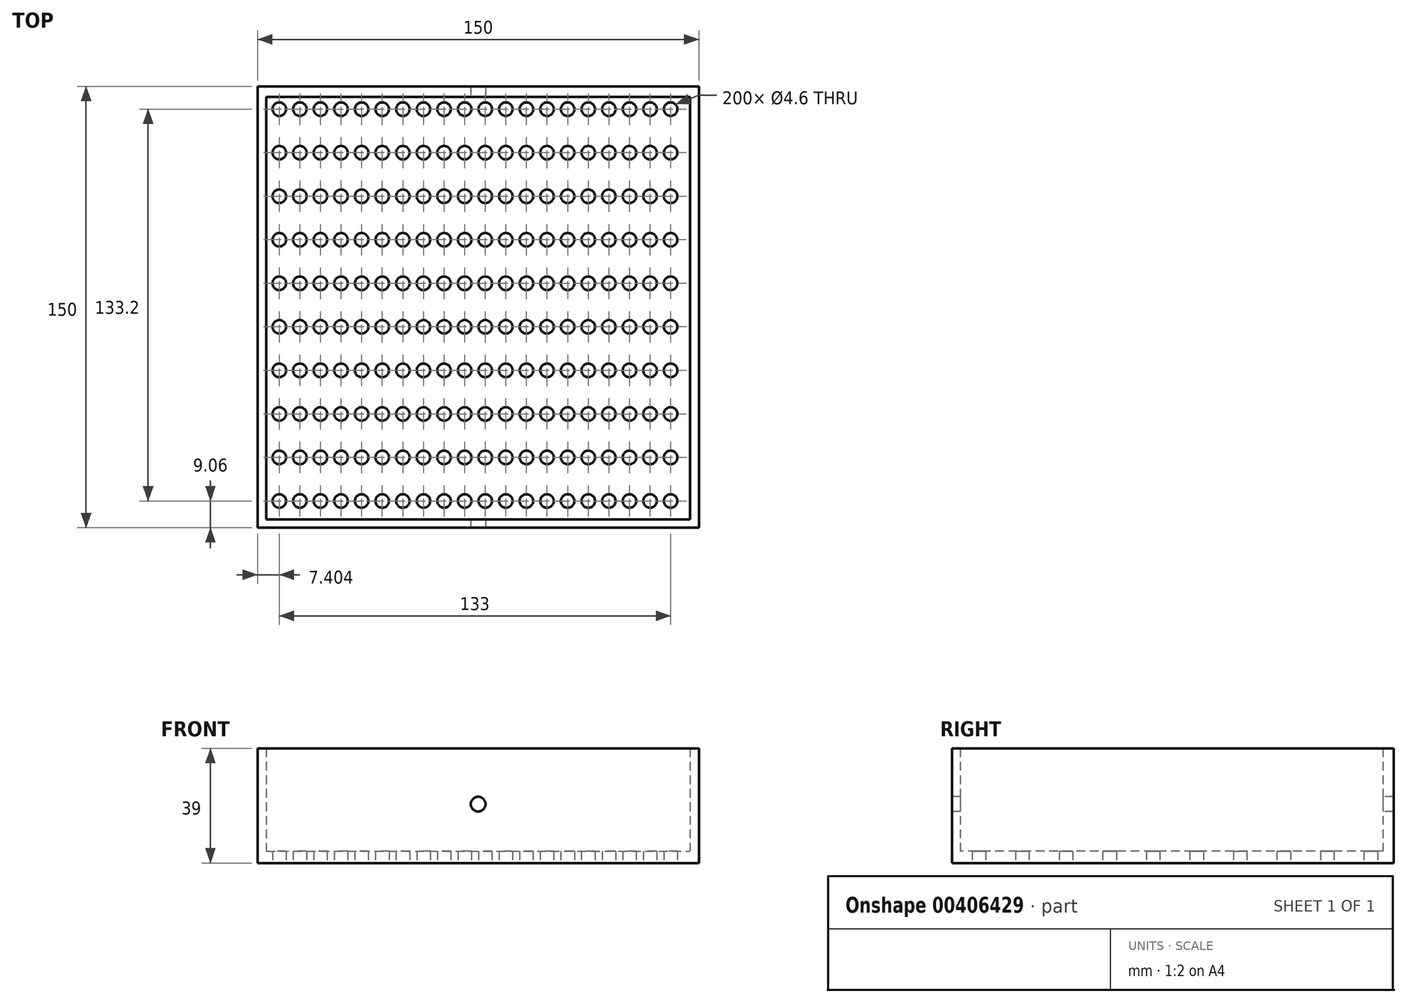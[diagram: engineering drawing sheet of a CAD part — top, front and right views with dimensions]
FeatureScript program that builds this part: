
annotation { "Feature Type Name" : "Feature", "Feature Type Description" : "" }
export const myFeature = defineFeature(function(context is Context, id is Id, definition is map)
    precondition{}
    {
        {
            var Q0;
            Q0=qCreatedBy(makeId("Top.planeOp"),FACE);
            var sketch = newSketch(context, id + "F0", { "sketchPlane" : qUnion([Q0])});
            skLineSegment(sketch, "E0.bottom", {"start": v(75, 75) * mm, "end": v(-75, 75) * mm});
            skLineSegment(sketch, "E0.top", {"start": v(75, -75) * mm, "end": v(-75, -75) * mm});
            skLineSegment(sketch, "E0.left", {"start": v(75, 75) * mm, "end": v(75, -75) * mm});
            skLineSegment(sketch, "E0.right", {"start": v(-75, 75) * mm, "end": v(-75, -75) * mm});
            skPoint(sketch, "E0.middle", {"position": v(0, 0) * mm});
            skCircle(sketch, "E1", {"center": v(-67.6, 67.26) * mm, "radius": 2.3 * mm});
            skCircle(sketch, "E2.0.1.0", {"center": v(-67.6, 52.46) * mm, "radius": 2.3 * mm});
            skCircle(sketch, "E2.0.2.0", {"center": v(-67.6, 37.66) * mm, "radius": 2.3 * mm});
            skCircle(sketch, "E2.0.3.0", {"center": v(-67.6, 22.86) * mm, "radius": 2.3 * mm});
            skCircle(sketch, "E2.0.4.0", {"center": v(-67.6, 8.06) * mm, "radius": 2.3 * mm});
            skCircle(sketch, "E2.0.5.0", {"center": v(-67.6, -6.74) * mm, "radius": 2.3 * mm});
            skCircle(sketch, "E2.0.6.0", {"center": v(-67.6, -21.54) * mm, "radius": 2.3 * mm});
            skCircle(sketch, "E2.0.7.0", {"center": v(-67.6, -36.34) * mm, "radius": 2.3 * mm});
            skCircle(sketch, "E2.0.8.0", {"center": v(-67.6, -51.14) * mm, "radius": 2.3 * mm});
            skCircle(sketch, "E2.0.9.0", {"center": v(-67.6, -65.94) * mm, "radius": 2.3 * mm});
            skCircle(sketch, "E2.1.0.0", {"center": v(-60.6, 67.26) * mm, "radius": 2.3 * mm});
            skCircle(sketch, "E2.1.1.0", {"center": v(-60.6, 52.46) * mm, "radius": 2.3 * mm});
            skCircle(sketch, "E2.1.2.0", {"center": v(-60.6, 37.66) * mm, "radius": 2.3 * mm});
            skCircle(sketch, "E2.1.3.0", {"center": v(-60.6, 22.86) * mm, "radius": 2.3 * mm});
            skCircle(sketch, "E2.1.4.0", {"center": v(-60.6, 8.06) * mm, "radius": 2.3 * mm});
            skCircle(sketch, "E2.1.5.0", {"center": v(-60.6, -6.74) * mm, "radius": 2.3 * mm});
            skCircle(sketch, "E2.1.6.0", {"center": v(-60.6, -21.54) * mm, "radius": 2.3 * mm});
            skCircle(sketch, "E2.1.7.0", {"center": v(-60.6, -36.34) * mm, "radius": 2.3 * mm});
            skCircle(sketch, "E2.1.8.0", {"center": v(-60.6, -51.14) * mm, "radius": 2.3 * mm});
            skCircle(sketch, "E2.1.9.0", {"center": v(-60.6, -65.94) * mm, "radius": 2.3 * mm});
            skCircle(sketch, "E2.2.0.0", {"center": v(-53.6, 67.26) * mm, "radius": 2.3 * mm});
            skCircle(sketch, "E2.2.1.0", {"center": v(-53.6, 52.46) * mm, "radius": 2.3 * mm});
            skCircle(sketch, "E2.2.2.0", {"center": v(-53.6, 37.66) * mm, "radius": 2.3 * mm});
            skCircle(sketch, "E2.2.3.0", {"center": v(-53.6, 22.86) * mm, "radius": 2.3 * mm});
            skCircle(sketch, "E2.2.4.0", {"center": v(-53.6, 8.06) * mm, "radius": 2.3 * mm});
            skCircle(sketch, "E2.2.5.0", {"center": v(-53.6, -6.74) * mm, "radius": 2.3 * mm});
            skCircle(sketch, "E2.2.6.0", {"center": v(-53.6, -21.54) * mm, "radius": 2.3 * mm});
            skCircle(sketch, "E2.2.7.0", {"center": v(-53.6, -36.34) * mm, "radius": 2.3 * mm});
            skCircle(sketch, "E2.2.8.0", {"center": v(-53.6, -51.14) * mm, "radius": 2.3 * mm});
            skCircle(sketch, "E2.2.9.0", {"center": v(-53.6, -65.94) * mm, "radius": 2.3 * mm});
            skCircle(sketch, "E2.3.0.0", {"center": v(-46.6, 67.26) * mm, "radius": 2.3 * mm});
            skCircle(sketch, "E2.3.1.0", {"center": v(-46.6, 52.46) * mm, "radius": 2.3 * mm});
            skCircle(sketch, "E2.3.2.0", {"center": v(-46.6, 37.66) * mm, "radius": 2.3 * mm});
            skCircle(sketch, "E2.3.3.0", {"center": v(-46.6, 22.86) * mm, "radius": 2.3 * mm});
            skCircle(sketch, "E2.3.4.0", {"center": v(-46.6, 8.06) * mm, "radius": 2.3 * mm});
            skCircle(sketch, "E2.3.5.0", {"center": v(-46.6, -6.74) * mm, "radius": 2.3 * mm});
            skCircle(sketch, "E2.3.6.0", {"center": v(-46.6, -21.54) * mm, "radius": 2.3 * mm});
            skCircle(sketch, "E2.3.7.0", {"center": v(-46.6, -36.34) * mm, "radius": 2.3 * mm});
            skCircle(sketch, "E2.3.8.0", {"center": v(-46.6, -51.14) * mm, "radius": 2.3 * mm});
            skCircle(sketch, "E2.3.9.0", {"center": v(-46.6, -65.94) * mm, "radius": 2.3 * mm});
            skCircle(sketch, "E2.4.0.0", {"center": v(-39.6, 67.26) * mm, "radius": 2.3 * mm});
            skCircle(sketch, "E2.4.1.0", {"center": v(-39.6, 52.46) * mm, "radius": 2.3 * mm});
            skCircle(sketch, "E2.4.2.0", {"center": v(-39.6, 37.66) * mm, "radius": 2.3 * mm});
            skCircle(sketch, "E2.4.3.0", {"center": v(-39.6, 22.86) * mm, "radius": 2.3 * mm});
            skCircle(sketch, "E2.4.4.0", {"center": v(-39.6, 8.06) * mm, "radius": 2.3 * mm});
            skCircle(sketch, "E2.4.5.0", {"center": v(-39.6, -6.74) * mm, "radius": 2.3 * mm});
            skCircle(sketch, "E2.4.6.0", {"center": v(-39.6, -21.54) * mm, "radius": 2.3 * mm});
            skCircle(sketch, "E2.4.7.0", {"center": v(-39.6, -36.34) * mm, "radius": 2.3 * mm});
            skCircle(sketch, "E2.4.8.0", {"center": v(-39.6, -51.14) * mm, "radius": 2.3 * mm});
            skCircle(sketch, "E2.4.9.0", {"center": v(-39.6, -65.94) * mm, "radius": 2.3 * mm});
            skCircle(sketch, "E2.5.0.0", {"center": v(-32.6, 67.26) * mm, "radius": 2.3 * mm});
            skCircle(sketch, "E2.5.1.0", {"center": v(-32.6, 52.46) * mm, "radius": 2.3 * mm});
            skCircle(sketch, "E2.5.2.0", {"center": v(-32.6, 37.66) * mm, "radius": 2.3 * mm});
            skCircle(sketch, "E2.5.3.0", {"center": v(-32.6, 22.86) * mm, "radius": 2.3 * mm});
            skCircle(sketch, "E2.5.4.0", {"center": v(-32.6, 8.06) * mm, "radius": 2.3 * mm});
            skCircle(sketch, "E2.5.5.0", {"center": v(-32.6, -6.74) * mm, "radius": 2.3 * mm});
            skCircle(sketch, "E2.5.6.0", {"center": v(-32.6, -21.54) * mm, "radius": 2.3 * mm});
            skCircle(sketch, "E2.5.7.0", {"center": v(-32.6, -36.34) * mm, "radius": 2.3 * mm});
            skCircle(sketch, "E2.5.8.0", {"center": v(-32.6, -51.14) * mm, "radius": 2.3 * mm});
            skCircle(sketch, "E2.5.9.0", {"center": v(-32.6, -65.94) * mm, "radius": 2.3 * mm});
            skCircle(sketch, "E2.6.0.0", {"center": v(-25.6, 67.26) * mm, "radius": 2.3 * mm});
            skCircle(sketch, "E2.6.1.0", {"center": v(-25.6, 52.46) * mm, "radius": 2.3 * mm});
            skCircle(sketch, "E2.6.2.0", {"center": v(-25.6, 37.66) * mm, "radius": 2.3 * mm});
            skCircle(sketch, "E2.6.3.0", {"center": v(-25.6, 22.86) * mm, "radius": 2.3 * mm});
            skCircle(sketch, "E2.6.4.0", {"center": v(-25.6, 8.06) * mm, "radius": 2.3 * mm});
            skCircle(sketch, "E2.6.5.0", {"center": v(-25.6, -6.74) * mm, "radius": 2.3 * mm});
            skCircle(sketch, "E2.6.6.0", {"center": v(-25.6, -21.54) * mm, "radius": 2.3 * mm});
            skCircle(sketch, "E2.6.7.0", {"center": v(-25.6, -36.34) * mm, "radius": 2.3 * mm});
            skCircle(sketch, "E2.6.8.0", {"center": v(-25.6, -51.14) * mm, "radius": 2.3 * mm});
            skCircle(sketch, "E2.6.9.0", {"center": v(-25.6, -65.94) * mm, "radius": 2.3 * mm});
            skCircle(sketch, "E2.7.0.0", {"center": v(-18.6, 67.26) * mm, "radius": 2.3 * mm});
            skCircle(sketch, "E2.7.1.0", {"center": v(-18.6, 52.46) * mm, "radius": 2.3 * mm});
            skCircle(sketch, "E2.7.2.0", {"center": v(-18.6, 37.66) * mm, "radius": 2.3 * mm});
            skCircle(sketch, "E2.7.3.0", {"center": v(-18.6, 22.86) * mm, "radius": 2.3 * mm});
            skCircle(sketch, "E2.7.4.0", {"center": v(-18.6, 8.06) * mm, "radius": 2.3 * mm});
            skCircle(sketch, "E2.7.5.0", {"center": v(-18.6, -6.74) * mm, "radius": 2.3 * mm});
            skCircle(sketch, "E2.7.6.0", {"center": v(-18.6, -21.54) * mm, "radius": 2.3 * mm});
            skCircle(sketch, "E2.7.7.0", {"center": v(-18.6, -36.34) * mm, "radius": 2.3 * mm});
            skCircle(sketch, "E2.7.8.0", {"center": v(-18.6, -51.14) * mm, "radius": 2.3 * mm});
            skCircle(sketch, "E2.7.9.0", {"center": v(-18.6, -65.94) * mm, "radius": 2.3 * mm});
            skCircle(sketch, "E2.8.0.0", {"center": v(-11.6, 67.26) * mm, "radius": 2.3 * mm});
            skCircle(sketch, "E2.8.1.0", {"center": v(-11.6, 52.46) * mm, "radius": 2.3 * mm});
            skCircle(sketch, "E2.8.2.0", {"center": v(-11.6, 37.66) * mm, "radius": 2.3 * mm});
            skCircle(sketch, "E2.8.3.0", {"center": v(-11.6, 22.86) * mm, "radius": 2.3 * mm});
            skCircle(sketch, "E2.8.4.0", {"center": v(-11.6, 8.06) * mm, "radius": 2.3 * mm});
            skCircle(sketch, "E2.8.5.0", {"center": v(-11.6, -6.74) * mm, "radius": 2.3 * mm});
            skCircle(sketch, "E2.8.6.0", {"center": v(-11.6, -21.54) * mm, "radius": 2.3 * mm});
            skCircle(sketch, "E2.8.7.0", {"center": v(-11.6, -36.34) * mm, "radius": 2.3 * mm});
            skCircle(sketch, "E2.8.8.0", {"center": v(-11.6, -51.14) * mm, "radius": 2.3 * mm});
            skCircle(sketch, "E2.8.9.0", {"center": v(-11.6, -65.94) * mm, "radius": 2.3 * mm});
            skCircle(sketch, "E2.9.0.0", {"center": v(-4.6, 67.26) * mm, "radius": 2.3 * mm});
            skCircle(sketch, "E2.9.1.0", {"center": v(-4.6, 52.46) * mm, "radius": 2.3 * mm});
            skCircle(sketch, "E2.9.2.0", {"center": v(-4.6, 37.66) * mm, "radius": 2.3 * mm});
            skCircle(sketch, "E2.9.3.0", {"center": v(-4.6, 22.86) * mm, "radius": 2.3 * mm});
            skCircle(sketch, "E2.9.4.0", {"center": v(-4.6, 8.06) * mm, "radius": 2.3 * mm});
            skCircle(sketch, "E2.9.5.0", {"center": v(-4.6, -6.74) * mm, "radius": 2.3 * mm});
            skCircle(sketch, "E2.9.6.0", {"center": v(-4.6, -21.54) * mm, "radius": 2.3 * mm});
            skCircle(sketch, "E2.9.7.0", {"center": v(-4.6, -36.34) * mm, "radius": 2.3 * mm});
            skCircle(sketch, "E2.9.8.0", {"center": v(-4.6, -51.14) * mm, "radius": 2.3 * mm});
            skCircle(sketch, "E2.9.9.0", {"center": v(-4.6, -65.94) * mm, "radius": 2.3 * mm});
            skCircle(sketch, "E2.10.0.0", {"center": v(2.4, 67.26) * mm, "radius": 2.3 * mm});
            skCircle(sketch, "E2.10.1.0", {"center": v(2.4, 52.46) * mm, "radius": 2.3 * mm});
            skCircle(sketch, "E2.10.2.0", {"center": v(2.4, 37.66) * mm, "radius": 2.3 * mm});
            skCircle(sketch, "E2.10.3.0", {"center": v(2.4, 22.86) * mm, "radius": 2.3 * mm});
            skCircle(sketch, "E2.10.4.0", {"center": v(2.4, 8.06) * mm, "radius": 2.3 * mm});
            skCircle(sketch, "E2.10.5.0", {"center": v(2.4, -6.74) * mm, "radius": 2.3 * mm});
            skCircle(sketch, "E2.10.6.0", {"center": v(2.4, -21.54) * mm, "radius": 2.3 * mm});
            skCircle(sketch, "E2.10.7.0", {"center": v(2.4, -36.34) * mm, "radius": 2.3 * mm});
            skCircle(sketch, "E2.10.8.0", {"center": v(2.4, -51.14) * mm, "radius": 2.3 * mm});
            skCircle(sketch, "E2.10.9.0", {"center": v(2.4, -65.94) * mm, "radius": 2.3 * mm});
            skCircle(sketch, "E2.11.0.0", {"center": v(9.4, 67.26) * mm, "radius": 2.3 * mm});
            skCircle(sketch, "E2.11.1.0", {"center": v(9.4, 52.46) * mm, "radius": 2.3 * mm});
            skCircle(sketch, "E2.11.2.0", {"center": v(9.4, 37.66) * mm, "radius": 2.3 * mm});
            skCircle(sketch, "E2.11.3.0", {"center": v(9.4, 22.86) * mm, "radius": 2.3 * mm});
            skCircle(sketch, "E2.11.4.0", {"center": v(9.4, 8.06) * mm, "radius": 2.3 * mm});
            skCircle(sketch, "E2.11.5.0", {"center": v(9.4, -6.74) * mm, "radius": 2.3 * mm});
            skCircle(sketch, "E2.11.6.0", {"center": v(9.4, -21.54) * mm, "radius": 2.3 * mm});
            skCircle(sketch, "E2.11.7.0", {"center": v(9.4, -36.34) * mm, "radius": 2.3 * mm});
            skCircle(sketch, "E2.11.8.0", {"center": v(9.4, -51.14) * mm, "radius": 2.3 * mm});
            skCircle(sketch, "E2.11.9.0", {"center": v(9.4, -65.94) * mm, "radius": 2.3 * mm});
            skCircle(sketch, "E2.12.0.0", {"center": v(16.4, 67.26) * mm, "radius": 2.3 * mm});
            skCircle(sketch, "E2.12.1.0", {"center": v(16.4, 52.46) * mm, "radius": 2.3 * mm});
            skCircle(sketch, "E2.12.2.0", {"center": v(16.4, 37.66) * mm, "radius": 2.3 * mm});
            skCircle(sketch, "E2.12.3.0", {"center": v(16.4, 22.86) * mm, "radius": 2.3 * mm});
            skCircle(sketch, "E2.12.4.0", {"center": v(16.4, 8.06) * mm, "radius": 2.3 * mm});
            skCircle(sketch, "E2.12.5.0", {"center": v(16.4, -6.74) * mm, "radius": 2.3 * mm});
            skCircle(sketch, "E2.12.6.0", {"center": v(16.4, -21.54) * mm, "radius": 2.3 * mm});
            skCircle(sketch, "E2.12.7.0", {"center": v(16.4, -36.34) * mm, "radius": 2.3 * mm});
            skCircle(sketch, "E2.12.8.0", {"center": v(16.4, -51.14) * mm, "radius": 2.3 * mm});
            skCircle(sketch, "E2.12.9.0", {"center": v(16.4, -65.94) * mm, "radius": 2.3 * mm});
            skCircle(sketch, "E2.13.0.0", {"center": v(23.4, 67.26) * mm, "radius": 2.3 * mm});
            skCircle(sketch, "E2.13.1.0", {"center": v(23.4, 52.46) * mm, "radius": 2.3 * mm});
            skCircle(sketch, "E2.13.2.0", {"center": v(23.4, 37.66) * mm, "radius": 2.3 * mm});
            skCircle(sketch, "E2.13.3.0", {"center": v(23.4, 22.86) * mm, "radius": 2.3 * mm});
            skCircle(sketch, "E2.13.4.0", {"center": v(23.4, 8.06) * mm, "radius": 2.3 * mm});
            skCircle(sketch, "E2.13.5.0", {"center": v(23.4, -6.74) * mm, "radius": 2.3 * mm});
            skCircle(sketch, "E2.13.6.0", {"center": v(23.4, -21.54) * mm, "radius": 2.3 * mm});
            skCircle(sketch, "E2.13.7.0", {"center": v(23.4, -36.34) * mm, "radius": 2.3 * mm});
            skCircle(sketch, "E2.13.8.0", {"center": v(23.4, -51.14) * mm, "radius": 2.3 * mm});
            skCircle(sketch, "E2.13.9.0", {"center": v(23.4, -65.94) * mm, "radius": 2.3 * mm});
            skCircle(sketch, "E2.14.0.0", {"center": v(30.4, 67.26) * mm, "radius": 2.3 * mm});
            skCircle(sketch, "E2.14.1.0", {"center": v(30.4, 52.46) * mm, "radius": 2.3 * mm});
            skCircle(sketch, "E2.14.2.0", {"center": v(30.4, 37.66) * mm, "radius": 2.3 * mm});
            skCircle(sketch, "E2.14.3.0", {"center": v(30.4, 22.86) * mm, "radius": 2.3 * mm});
            skCircle(sketch, "E2.14.4.0", {"center": v(30.4, 8.06) * mm, "radius": 2.3 * mm});
            skCircle(sketch, "E2.14.5.0", {"center": v(30.4, -6.74) * mm, "radius": 2.3 * mm});
            skCircle(sketch, "E2.14.6.0", {"center": v(30.4, -21.54) * mm, "radius": 2.3 * mm});
            skCircle(sketch, "E2.14.7.0", {"center": v(30.4, -36.34) * mm, "radius": 2.3 * mm});
            skCircle(sketch, "E2.14.8.0", {"center": v(30.4, -51.14) * mm, "radius": 2.3 * mm});
            skCircle(sketch, "E2.14.9.0", {"center": v(30.4, -65.94) * mm, "radius": 2.3 * mm});
            skCircle(sketch, "E2.15.0.0", {"center": v(37.4, 67.26) * mm, "radius": 2.3 * mm});
            skCircle(sketch, "E2.15.1.0", {"center": v(37.4, 52.46) * mm, "radius": 2.3 * mm});
            skCircle(sketch, "E2.15.2.0", {"center": v(37.4, 37.66) * mm, "radius": 2.3 * mm});
            skCircle(sketch, "E2.15.3.0", {"center": v(37.4, 22.86) * mm, "radius": 2.3 * mm});
            skCircle(sketch, "E2.15.4.0", {"center": v(37.4, 8.06) * mm, "radius": 2.3 * mm});
            skCircle(sketch, "E2.15.5.0", {"center": v(37.4, -6.74) * mm, "radius": 2.3 * mm});
            skCircle(sketch, "E2.15.6.0", {"center": v(37.4, -21.54) * mm, "radius": 2.3 * mm});
            skCircle(sketch, "E2.15.7.0", {"center": v(37.4, -36.34) * mm, "radius": 2.3 * mm});
            skCircle(sketch, "E2.15.8.0", {"center": v(37.4, -51.14) * mm, "radius": 2.3 * mm});
            skCircle(sketch, "E2.15.9.0", {"center": v(37.4, -65.94) * mm, "radius": 2.3 * mm});
            skCircle(sketch, "E2.16.0.0", {"center": v(44.4, 67.26) * mm, "radius": 2.3 * mm});
            skCircle(sketch, "E2.16.1.0", {"center": v(44.4, 52.46) * mm, "radius": 2.3 * mm});
            skCircle(sketch, "E2.16.2.0", {"center": v(44.4, 37.66) * mm, "radius": 2.3 * mm});
            skCircle(sketch, "E2.16.3.0", {"center": v(44.4, 22.86) * mm, "radius": 2.3 * mm});
            skCircle(sketch, "E2.16.4.0", {"center": v(44.4, 8.06) * mm, "radius": 2.3 * mm});
            skCircle(sketch, "E2.16.5.0", {"center": v(44.4, -6.74) * mm, "radius": 2.3 * mm});
            skCircle(sketch, "E2.16.6.0", {"center": v(44.4, -21.54) * mm, "radius": 2.3 * mm});
            skCircle(sketch, "E2.16.7.0", {"center": v(44.4, -36.34) * mm, "radius": 2.3 * mm});
            skCircle(sketch, "E2.16.8.0", {"center": v(44.4, -51.14) * mm, "radius": 2.3 * mm});
            skCircle(sketch, "E2.16.9.0", {"center": v(44.4, -65.94) * mm, "radius": 2.3 * mm});
            skCircle(sketch, "E2.17.0.0", {"center": v(51.4, 67.26) * mm, "radius": 2.3 * mm});
            skCircle(sketch, "E2.17.1.0", {"center": v(51.4, 52.46) * mm, "radius": 2.3 * mm});
            skCircle(sketch, "E2.17.2.0", {"center": v(51.4, 37.66) * mm, "radius": 2.3 * mm});
            skCircle(sketch, "E2.17.3.0", {"center": v(51.4, 22.86) * mm, "radius": 2.3 * mm});
            skCircle(sketch, "E2.17.4.0", {"center": v(51.4, 8.06) * mm, "radius": 2.3 * mm});
            skCircle(sketch, "E2.17.5.0", {"center": v(51.4, -6.74) * mm, "radius": 2.3 * mm});
            skCircle(sketch, "E2.17.6.0", {"center": v(51.4, -21.54) * mm, "radius": 2.3 * mm});
            skCircle(sketch, "E2.17.7.0", {"center": v(51.4, -36.34) * mm, "radius": 2.3 * mm});
            skCircle(sketch, "E2.17.8.0", {"center": v(51.4, -51.14) * mm, "radius": 2.3 * mm});
            skCircle(sketch, "E2.17.9.0", {"center": v(51.4, -65.94) * mm, "radius": 2.3 * mm});
            skCircle(sketch, "E2.18.0.0", {"center": v(58.4, 67.26) * mm, "radius": 2.3 * mm});
            skCircle(sketch, "E2.18.1.0", {"center": v(58.4, 52.46) * mm, "radius": 2.3 * mm});
            skCircle(sketch, "E2.18.2.0", {"center": v(58.4, 37.66) * mm, "radius": 2.3 * mm});
            skCircle(sketch, "E2.18.3.0", {"center": v(58.4, 22.86) * mm, "radius": 2.3 * mm});
            skCircle(sketch, "E2.18.4.0", {"center": v(58.4, 8.06) * mm, "radius": 2.3 * mm});
            skCircle(sketch, "E2.18.5.0", {"center": v(58.4, -6.74) * mm, "radius": 2.3 * mm});
            skCircle(sketch, "E2.18.6.0", {"center": v(58.4, -21.54) * mm, "radius": 2.3 * mm});
            skCircle(sketch, "E2.18.7.0", {"center": v(58.4, -36.34) * mm, "radius": 2.3 * mm});
            skCircle(sketch, "E2.18.8.0", {"center": v(58.4, -51.14) * mm, "radius": 2.3 * mm});
            skCircle(sketch, "E2.18.9.0", {"center": v(58.4, -65.94) * mm, "radius": 2.3 * mm});
            skCircle(sketch, "E2.19.0.0", {"center": v(65.4, 67.26) * mm, "radius": 2.3 * mm});
            skCircle(sketch, "E2.19.1.0", {"center": v(65.4, 52.46) * mm, "radius": 2.3 * mm});
            skCircle(sketch, "E2.19.2.0", {"center": v(65.4, 37.66) * mm, "radius": 2.3 * mm});
            skCircle(sketch, "E2.19.3.0", {"center": v(65.4, 22.86) * mm, "radius": 2.3 * mm});
            skCircle(sketch, "E2.19.4.0", {"center": v(65.4, 8.06) * mm, "radius": 2.3 * mm});
            skCircle(sketch, "E2.19.5.0", {"center": v(65.4, -6.74) * mm, "radius": 2.3 * mm});
            skCircle(sketch, "E2.19.6.0", {"center": v(65.4, -21.54) * mm, "radius": 2.3 * mm});
            skCircle(sketch, "E2.19.7.0", {"center": v(65.4, -36.34) * mm, "radius": 2.3 * mm});
            skCircle(sketch, "E2.19.8.0", {"center": v(65.4, -51.14) * mm, "radius": 2.3 * mm});
            skCircle(sketch, "E2.19.9.0", {"center": v(65.4, -65.94) * mm, "radius": 2.3 * mm});
            skLineSegment(sketch, "E2.direction1", {"start": v(-67.6, 67.26) * mm, "end": v(-60.6, 67.26) * mm, "construction": true});
            skLineSegment(sketch, "E2.direction2", {"start": v(-67.6, 67.26) * mm, "end": v(-67.6, 52.46) * mm, "construction": true});
            skSolve(sketch);
        }
        {
            var Q0;
            Q0=makeQuery(id+"F0.imprint","IMPRINT",FACE,{"disambiguationData":[TD([[makeQuery(id+"F0.imprint","IMPRINT",EDGE,{"derivedFrom":sQuery(id+"F0.wireOp",EDGE,"E0.bottom")}),1.0]])]});
            extrude(context, id + "F1", {"entities" : qUnion([Q0]), "depth" : 4 * mm});
        }
        {
            var Q0;
            Q0=makeQuery(id+"F1.opExtrude","CAP_FACE",FACE,{"disambiguationData":[OSD([sQuery(id+"F0.wireOp",EDGE,"E0.bottom"),sQuery(id+"F0.wireOp",EDGE,"E0.top"),sQuery(id+"F0.wireOp",EDGE,"E0.left"),sQuery(id+"F0.wireOp",EDGE,"E0.right"),sQuery(id+"F0.wireOp",EDGE,"E1"),sQuery(id+"F0.wireOp",EDGE,"E2.0.1.0"),sQuery(id+"F0.wireOp",EDGE,"E2.0.2.0"),sQuery(id+"F0.wireOp",EDGE,"E2.0.3.0"),sQuery(id+"F0.wireOp",EDGE,"E2.0.4.0"),sQuery(id+"F0.wireOp",EDGE,"E2.0.5.0"),sQuery(id+"F0.wireOp",EDGE,"E2.0.6.0"),sQuery(id+"F0.wireOp",EDGE,"E2.0.7.0"),sQuery(id+"F0.wireOp",EDGE,"E2.0.8.0"),sQuery(id+"F0.wireOp",EDGE,"E2.0.9.0"),sQuery(id+"F0.wireOp",EDGE,"E2.1.0.0"),sQuery(id+"F0.wireOp",EDGE,"E2.1.1.0"),sQuery(id+"F0.wireOp",EDGE,"E2.1.2.0"),sQuery(id+"F0.wireOp",EDGE,"E2.1.3.0"),sQuery(id+"F0.wireOp",EDGE,"E2.1.4.0"),sQuery(id+"F0.wireOp",EDGE,"E2.1.5.0"),sQuery(id+"F0.wireOp",EDGE,"E2.1.6.0"),sQuery(id+"F0.wireOp",EDGE,"E2.1.7.0"),sQuery(id+"F0.wireOp",EDGE,"E2.1.8.0"),sQuery(id+"F0.wireOp",EDGE,"E2.1.9.0"),sQuery(id+"F0.wireOp",EDGE,"E2.2.0.0"),sQuery(id+"F0.wireOp",EDGE,"E2.2.1.0"),sQuery(id+"F0.wireOp",EDGE,"E2.2.2.0"),sQuery(id+"F0.wireOp",EDGE,"E2.2.3.0"),sQuery(id+"F0.wireOp",EDGE,"E2.2.4.0"),sQuery(id+"F0.wireOp",EDGE,"E2.2.5.0"),sQuery(id+"F0.wireOp",EDGE,"E2.2.6.0"),sQuery(id+"F0.wireOp",EDGE,"E2.2.7.0"),sQuery(id+"F0.wireOp",EDGE,"E2.2.8.0"),sQuery(id+"F0.wireOp",EDGE,"E2.2.9.0"),sQuery(id+"F0.wireOp",EDGE,"E2.3.0.0"),sQuery(id+"F0.wireOp",EDGE,"E2.3.1.0"),sQuery(id+"F0.wireOp",EDGE,"E2.3.2.0"),sQuery(id+"F0.wireOp",EDGE,"E2.3.3.0"),sQuery(id+"F0.wireOp",EDGE,"E2.3.4.0"),sQuery(id+"F0.wireOp",EDGE,"E2.3.5.0"),sQuery(id+"F0.wireOp",EDGE,"E2.3.6.0"),sQuery(id+"F0.wireOp",EDGE,"E2.3.7.0"),sQuery(id+"F0.wireOp",EDGE,"E2.3.8.0"),sQuery(id+"F0.wireOp",EDGE,"E2.3.9.0"),sQuery(id+"F0.wireOp",EDGE,"E2.4.0.0"),sQuery(id+"F0.wireOp",EDGE,"E2.4.1.0"),sQuery(id+"F0.wireOp",EDGE,"E2.4.2.0"),sQuery(id+"F0.wireOp",EDGE,"E2.4.3.0"),sQuery(id+"F0.wireOp",EDGE,"E2.4.4.0"),sQuery(id+"F0.wireOp",EDGE,"E2.4.5.0"),sQuery(id+"F0.wireOp",EDGE,"E2.4.6.0"),sQuery(id+"F0.wireOp",EDGE,"E2.4.7.0"),sQuery(id+"F0.wireOp",EDGE,"E2.4.8.0"),sQuery(id+"F0.wireOp",EDGE,"E2.4.9.0"),sQuery(id+"F0.wireOp",EDGE,"E2.5.0.0"),sQuery(id+"F0.wireOp",EDGE,"E2.5.1.0"),sQuery(id+"F0.wireOp",EDGE,"E2.5.2.0"),sQuery(id+"F0.wireOp",EDGE,"E2.5.3.0"),sQuery(id+"F0.wireOp",EDGE,"E2.5.4.0"),sQuery(id+"F0.wireOp",EDGE,"E2.5.5.0"),sQuery(id+"F0.wireOp",EDGE,"E2.5.6.0"),sQuery(id+"F0.wireOp",EDGE,"E2.5.7.0"),sQuery(id+"F0.wireOp",EDGE,"E2.5.8.0"),sQuery(id+"F0.wireOp",EDGE,"E2.5.9.0"),sQuery(id+"F0.wireOp",EDGE,"E2.6.0.0"),sQuery(id+"F0.wireOp",EDGE,"E2.6.1.0"),sQuery(id+"F0.wireOp",EDGE,"E2.6.2.0"),sQuery(id+"F0.wireOp",EDGE,"E2.6.3.0"),sQuery(id+"F0.wireOp",EDGE,"E2.6.4.0"),sQuery(id+"F0.wireOp",EDGE,"E2.6.5.0"),sQuery(id+"F0.wireOp",EDGE,"E2.6.6.0"),sQuery(id+"F0.wireOp",EDGE,"E2.6.7.0"),sQuery(id+"F0.wireOp",EDGE,"E2.6.8.0"),sQuery(id+"F0.wireOp",EDGE,"E2.6.9.0"),sQuery(id+"F0.wireOp",EDGE,"E2.7.0.0"),sQuery(id+"F0.wireOp",EDGE,"E2.7.1.0"),sQuery(id+"F0.wireOp",EDGE,"E2.7.2.0"),sQuery(id+"F0.wireOp",EDGE,"E2.7.3.0"),sQuery(id+"F0.wireOp",EDGE,"E2.7.4.0"),sQuery(id+"F0.wireOp",EDGE,"E2.7.5.0"),sQuery(id+"F0.wireOp",EDGE,"E2.7.6.0"),sQuery(id+"F0.wireOp",EDGE,"E2.7.7.0"),sQuery(id+"F0.wireOp",EDGE,"E2.7.8.0"),sQuery(id+"F0.wireOp",EDGE,"E2.7.9.0"),sQuery(id+"F0.wireOp",EDGE,"E2.8.0.0"),sQuery(id+"F0.wireOp",EDGE,"E2.8.1.0"),sQuery(id+"F0.wireOp",EDGE,"E2.8.2.0"),sQuery(id+"F0.wireOp",EDGE,"E2.8.3.0"),sQuery(id+"F0.wireOp",EDGE,"E2.8.4.0"),sQuery(id+"F0.wireOp",EDGE,"E2.8.5.0"),sQuery(id+"F0.wireOp",EDGE,"E2.8.6.0"),sQuery(id+"F0.wireOp",EDGE,"E2.8.7.0"),sQuery(id+"F0.wireOp",EDGE,"E2.8.8.0"),sQuery(id+"F0.wireOp",EDGE,"E2.8.9.0"),sQuery(id+"F0.wireOp",EDGE,"E2.9.0.0"),sQuery(id+"F0.wireOp",EDGE,"E2.9.1.0"),sQuery(id+"F0.wireOp",EDGE,"E2.9.2.0"),sQuery(id+"F0.wireOp",EDGE,"E2.9.3.0"),sQuery(id+"F0.wireOp",EDGE,"E2.9.4.0"),sQuery(id+"F0.wireOp",EDGE,"E2.9.5.0"),sQuery(id+"F0.wireOp",EDGE,"E2.9.6.0"),sQuery(id+"F0.wireOp",EDGE,"E2.9.7.0"),sQuery(id+"F0.wireOp",EDGE,"E2.9.8.0"),sQuery(id+"F0.wireOp",EDGE,"E2.9.9.0"),sQuery(id+"F0.wireOp",EDGE,"E2.10.0.0"),sQuery(id+"F0.wireOp",EDGE,"E2.10.1.0"),sQuery(id+"F0.wireOp",EDGE,"E2.10.2.0"),sQuery(id+"F0.wireOp",EDGE,"E2.10.3.0"),sQuery(id+"F0.wireOp",EDGE,"E2.10.4.0"),sQuery(id+"F0.wireOp",EDGE,"E2.10.5.0"),sQuery(id+"F0.wireOp",EDGE,"E2.10.6.0"),sQuery(id+"F0.wireOp",EDGE,"E2.10.7.0"),sQuery(id+"F0.wireOp",EDGE,"E2.10.8.0"),sQuery(id+"F0.wireOp",EDGE,"E2.10.9.0"),sQuery(id+"F0.wireOp",EDGE,"E2.11.0.0"),sQuery(id+"F0.wireOp",EDGE,"E2.11.1.0"),sQuery(id+"F0.wireOp",EDGE,"E2.11.2.0"),sQuery(id+"F0.wireOp",EDGE,"E2.11.3.0"),sQuery(id+"F0.wireOp",EDGE,"E2.11.4.0"),sQuery(id+"F0.wireOp",EDGE,"E2.11.5.0"),sQuery(id+"F0.wireOp",EDGE,"E2.11.6.0"),sQuery(id+"F0.wireOp",EDGE,"E2.11.7.0"),sQuery(id+"F0.wireOp",EDGE,"E2.11.8.0"),sQuery(id+"F0.wireOp",EDGE,"E2.11.9.0"),sQuery(id+"F0.wireOp",EDGE,"E2.12.0.0"),sQuery(id+"F0.wireOp",EDGE,"E2.12.1.0"),sQuery(id+"F0.wireOp",EDGE,"E2.12.2.0"),sQuery(id+"F0.wireOp",EDGE,"E2.12.3.0"),sQuery(id+"F0.wireOp",EDGE,"E2.12.4.0"),sQuery(id+"F0.wireOp",EDGE,"E2.12.5.0"),sQuery(id+"F0.wireOp",EDGE,"E2.12.6.0"),sQuery(id+"F0.wireOp",EDGE,"E2.12.7.0"),sQuery(id+"F0.wireOp",EDGE,"E2.12.8.0"),sQuery(id+"F0.wireOp",EDGE,"E2.12.9.0"),sQuery(id+"F0.wireOp",EDGE,"E2.13.0.0"),sQuery(id+"F0.wireOp",EDGE,"E2.13.1.0"),sQuery(id+"F0.wireOp",EDGE,"E2.13.2.0"),sQuery(id+"F0.wireOp",EDGE,"E2.13.3.0"),sQuery(id+"F0.wireOp",EDGE,"E2.13.4.0"),sQuery(id+"F0.wireOp",EDGE,"E2.13.5.0"),sQuery(id+"F0.wireOp",EDGE,"E2.13.6.0"),sQuery(id+"F0.wireOp",EDGE,"E2.13.7.0"),sQuery(id+"F0.wireOp",EDGE,"E2.13.8.0"),sQuery(id+"F0.wireOp",EDGE,"E2.13.9.0"),sQuery(id+"F0.wireOp",EDGE,"E2.14.0.0"),sQuery(id+"F0.wireOp",EDGE,"E2.14.1.0"),sQuery(id+"F0.wireOp",EDGE,"E2.14.2.0"),sQuery(id+"F0.wireOp",EDGE,"E2.14.3.0"),sQuery(id+"F0.wireOp",EDGE,"E2.14.4.0"),sQuery(id+"F0.wireOp",EDGE,"E2.14.5.0"),sQuery(id+"F0.wireOp",EDGE,"E2.14.6.0"),sQuery(id+"F0.wireOp",EDGE,"E2.14.7.0"),sQuery(id+"F0.wireOp",EDGE,"E2.14.8.0"),sQuery(id+"F0.wireOp",EDGE,"E2.14.9.0"),sQuery(id+"F0.wireOp",EDGE,"E2.15.0.0"),sQuery(id+"F0.wireOp",EDGE,"E2.15.1.0"),sQuery(id+"F0.wireOp",EDGE,"E2.15.2.0"),sQuery(id+"F0.wireOp",EDGE,"E2.15.3.0"),sQuery(id+"F0.wireOp",EDGE,"E2.15.4.0"),sQuery(id+"F0.wireOp",EDGE,"E2.15.5.0"),sQuery(id+"F0.wireOp",EDGE,"E2.15.6.0"),sQuery(id+"F0.wireOp",EDGE,"E2.15.7.0"),sQuery(id+"F0.wireOp",EDGE,"E2.15.8.0"),sQuery(id+"F0.wireOp",EDGE,"E2.15.9.0"),sQuery(id+"F0.wireOp",EDGE,"E2.16.0.0"),sQuery(id+"F0.wireOp",EDGE,"E2.16.1.0"),sQuery(id+"F0.wireOp",EDGE,"E2.16.2.0"),sQuery(id+"F0.wireOp",EDGE,"E2.16.3.0"),sQuery(id+"F0.wireOp",EDGE,"E2.16.4.0"),sQuery(id+"F0.wireOp",EDGE,"E2.16.5.0"),sQuery(id+"F0.wireOp",EDGE,"E2.16.6.0"),sQuery(id+"F0.wireOp",EDGE,"E2.16.7.0"),sQuery(id+"F0.wireOp",EDGE,"E2.16.8.0"),sQuery(id+"F0.wireOp",EDGE,"E2.16.9.0"),sQuery(id+"F0.wireOp",EDGE,"E2.17.0.0"),sQuery(id+"F0.wireOp",EDGE,"E2.17.1.0"),sQuery(id+"F0.wireOp",EDGE,"E2.17.2.0"),sQuery(id+"F0.wireOp",EDGE,"E2.17.3.0"),sQuery(id+"F0.wireOp",EDGE,"E2.17.4.0"),sQuery(id+"F0.wireOp",EDGE,"E2.17.5.0"),sQuery(id+"F0.wireOp",EDGE,"E2.17.6.0"),sQuery(id+"F0.wireOp",EDGE,"E2.17.7.0"),sQuery(id+"F0.wireOp",EDGE,"E2.17.8.0"),sQuery(id+"F0.wireOp",EDGE,"E2.17.9.0"),sQuery(id+"F0.wireOp",EDGE,"E2.18.0.0"),sQuery(id+"F0.wireOp",EDGE,"E2.18.1.0"),sQuery(id+"F0.wireOp",EDGE,"E2.18.2.0"),sQuery(id+"F0.wireOp",EDGE,"E2.18.3.0"),sQuery(id+"F0.wireOp",EDGE,"E2.18.4.0"),sQuery(id+"F0.wireOp",EDGE,"E2.18.5.0"),sQuery(id+"F0.wireOp",EDGE,"E2.18.6.0"),sQuery(id+"F0.wireOp",EDGE,"E2.18.7.0"),sQuery(id+"F0.wireOp",EDGE,"E2.18.8.0"),sQuery(id+"F0.wireOp",EDGE,"E2.18.9.0"),sQuery(id+"F0.wireOp",EDGE,"E2.19.0.0"),sQuery(id+"F0.wireOp",EDGE,"E2.19.1.0"),sQuery(id+"F0.wireOp",EDGE,"E2.19.2.0"),sQuery(id+"F0.wireOp",EDGE,"E2.19.3.0"),sQuery(id+"F0.wireOp",EDGE,"E2.19.4.0"),sQuery(id+"F0.wireOp",EDGE,"E2.19.5.0"),sQuery(id+"F0.wireOp",EDGE,"E2.19.6.0"),sQuery(id+"F0.wireOp",EDGE,"E2.19.7.0"),sQuery(id+"F0.wireOp",EDGE,"E2.19.8.0"),sQuery(id+"F0.wireOp",EDGE,"E2.19.9.0")])],"isStart":false});
            var sketch = newSketch(context, id + "F2", { "sketchPlane" : qUnion([Q0])});
            skLineSegment(sketch, "E3.bottom", {"start": v(-75, 75) * mm, "end": v(-72, 75) * mm});
            skLineSegment(sketch, "E3.top", {"start": v(-75, -75) * mm, "end": v(-72, -75) * mm});
            skLineSegment(sketch, "E3.left", {"start": v(-75, 75) * mm, "end": v(-75, -75) * mm});
            skLineSegment(sketch, "E3.right", {"start": v(-72, 71.4) * mm, "end": v(-72, -72.24) * mm});
            skLineSegment(sketch, "E4.bottom", {"start": v(-75, -75) * mm, "end": v(75, -75) * mm});
            skLineSegment(sketch, "E4.top", {"start": v(-72, -72.24) * mm, "end": v(72, -72.24) * mm});
            skLineSegment(sketch, "E4.left", {"start": v(-75, -75) * mm, "end": v(-75, -72.24) * mm});
            skLineSegment(sketch, "E4.right", {"start": v(75, -75) * mm, "end": v(75, -72.24) * mm});
            skLineSegment(sketch, "E5.bottom", {"start": v(75, 75) * mm, "end": v(75, 75) * mm});
            skLineSegment(sketch, "E5.top", {"start": v(75, -75) * mm, "end": v(75, -75) * mm});
            skLineSegment(sketch, "E5.left", {"start": v(75, 75) * mm, "end": v(75, -75) * mm});
            skLineSegment(sketch, "E5.right", {"start": v(75, 75) * mm, "end": v(75, -75) * mm});
            skLineSegment(sketch, "E6.bottom", {"start": v(75, 75) * mm, "end": v(72, 75) * mm});
            skLineSegment(sketch, "E6.top", {"start": v(75, -75) * mm, "end": v(72, -75) * mm});
            skLineSegment(sketch, "E6.right", {"start": v(72, 71.4) * mm, "end": v(72, -72.24) * mm});
            skLineSegment(sketch, "E7.bottom", {"start": v(-75, 75) * mm, "end": v(75, 75) * mm});
            skLineSegment(sketch, "E7.top", {"start": v(-72, 71.4) * mm, "end": v(72, 71.4) * mm});
            skLineSegment(sketch, "E7.left", {"start": v(-75, 75) * mm, "end": v(-75, 71.4) * mm});
            skLineSegment(sketch, "E7.right", {"start": v(75, 75) * mm, "end": v(75, 71.4) * mm});
            skSolve(sketch);
        }
        {
            var Q0;
            Q0=makeQuery(id+"F2.imprint","IMPRINT",FACE,{"disambiguationData":[TD([[makeQuery(id+"F2.imprint","IMPRINT",EDGE,{"derivedFrom":sQuery(id+"F2.wireOp",EDGE,"E3.left")}),1.0]])]});
            extrude(context, id + "F3", {"entities" : qUnion([Q0]), "operationType" : NewBodyOperationType.ADD, "depth" : 35 * mm});
        }
        {
            var Q0;
            Q0=makeQuery(id+"F3.boolean.opBoolean","MERGE",FACE,{"derivedFrom":[makeQuery(id+"F1.opExtrude","SWEPT_FACE",FACE,{"disambiguationData":[OSD([sQuery(id+"F0.wireOp",EDGE,"E0.top")])]}),makeQuery(id+"F3.opExtrude","SWEPT_FACE",FACE,{"disambiguationData":[OSD([sQuery(id+"F2.wireOp",EDGE,"E4.bottom"),sQuery(id+"F2.wireOp",EDGE,"E6.top")])]})]});
            var sketch = newSketch(context, id + "F4", { "sketchPlane" : qUnion([Q0])});
            skCircle(sketch, "E8", {"center": v(0, 20.01) * mm, "radius": 3.31 * mm});
            skSolve(sketch);
        }
        {
            var Q0;
            Q0=sQuery(id+"F4.wireOp",VERTEX,"E8.center");
            var Q1;
            Q1=makeQuery(id+"F1.opExtrude","SWEPT_BODY",BODY,{"disambiguationData":[OSD([sQuery(id+"F0.wireOp",EDGE,"E0.bottom"),sQuery(id+"F0.wireOp",EDGE,"E0.top"),sQuery(id+"F0.wireOp",EDGE,"E0.left"),sQuery(id+"F0.wireOp",EDGE,"E0.right"),sQuery(id+"F0.wireOp",EDGE,"E1"),sQuery(id+"F0.wireOp",EDGE,"E2.0.1.0"),sQuery(id+"F0.wireOp",EDGE,"E2.0.2.0"),sQuery(id+"F0.wireOp",EDGE,"E2.0.3.0"),sQuery(id+"F0.wireOp",EDGE,"E2.0.4.0"),sQuery(id+"F0.wireOp",EDGE,"E2.0.5.0"),sQuery(id+"F0.wireOp",EDGE,"E2.0.6.0"),sQuery(id+"F0.wireOp",EDGE,"E2.0.7.0"),sQuery(id+"F0.wireOp",EDGE,"E2.0.8.0"),sQuery(id+"F0.wireOp",EDGE,"E2.0.9.0"),sQuery(id+"F0.wireOp",EDGE,"E2.1.0.0"),sQuery(id+"F0.wireOp",EDGE,"E2.1.1.0"),sQuery(id+"F0.wireOp",EDGE,"E2.1.2.0"),sQuery(id+"F0.wireOp",EDGE,"E2.1.3.0"),sQuery(id+"F0.wireOp",EDGE,"E2.1.4.0"),sQuery(id+"F0.wireOp",EDGE,"E2.1.5.0"),sQuery(id+"F0.wireOp",EDGE,"E2.1.6.0"),sQuery(id+"F0.wireOp",EDGE,"E2.1.7.0"),sQuery(id+"F0.wireOp",EDGE,"E2.1.8.0"),sQuery(id+"F0.wireOp",EDGE,"E2.1.9.0"),sQuery(id+"F0.wireOp",EDGE,"E2.2.0.0"),sQuery(id+"F0.wireOp",EDGE,"E2.2.1.0"),sQuery(id+"F0.wireOp",EDGE,"E2.2.2.0"),sQuery(id+"F0.wireOp",EDGE,"E2.2.3.0"),sQuery(id+"F0.wireOp",EDGE,"E2.2.4.0"),sQuery(id+"F0.wireOp",EDGE,"E2.2.5.0"),sQuery(id+"F0.wireOp",EDGE,"E2.2.6.0"),sQuery(id+"F0.wireOp",EDGE,"E2.2.7.0"),sQuery(id+"F0.wireOp",EDGE,"E2.2.8.0"),sQuery(id+"F0.wireOp",EDGE,"E2.2.9.0"),sQuery(id+"F0.wireOp",EDGE,"E2.3.0.0"),sQuery(id+"F0.wireOp",EDGE,"E2.3.1.0"),sQuery(id+"F0.wireOp",EDGE,"E2.3.2.0"),sQuery(id+"F0.wireOp",EDGE,"E2.3.3.0"),sQuery(id+"F0.wireOp",EDGE,"E2.3.4.0"),sQuery(id+"F0.wireOp",EDGE,"E2.3.5.0"),sQuery(id+"F0.wireOp",EDGE,"E2.3.6.0"),sQuery(id+"F0.wireOp",EDGE,"E2.3.7.0"),sQuery(id+"F0.wireOp",EDGE,"E2.3.8.0"),sQuery(id+"F0.wireOp",EDGE,"E2.3.9.0"),sQuery(id+"F0.wireOp",EDGE,"E2.4.0.0"),sQuery(id+"F0.wireOp",EDGE,"E2.4.1.0"),sQuery(id+"F0.wireOp",EDGE,"E2.4.2.0"),sQuery(id+"F0.wireOp",EDGE,"E2.4.3.0"),sQuery(id+"F0.wireOp",EDGE,"E2.4.4.0"),sQuery(id+"F0.wireOp",EDGE,"E2.4.5.0"),sQuery(id+"F0.wireOp",EDGE,"E2.4.6.0"),sQuery(id+"F0.wireOp",EDGE,"E2.4.7.0"),sQuery(id+"F0.wireOp",EDGE,"E2.4.8.0"),sQuery(id+"F0.wireOp",EDGE,"E2.4.9.0"),sQuery(id+"F0.wireOp",EDGE,"E2.5.0.0"),sQuery(id+"F0.wireOp",EDGE,"E2.5.1.0"),sQuery(id+"F0.wireOp",EDGE,"E2.5.2.0"),sQuery(id+"F0.wireOp",EDGE,"E2.5.3.0"),sQuery(id+"F0.wireOp",EDGE,"E2.5.4.0"),sQuery(id+"F0.wireOp",EDGE,"E2.5.5.0"),sQuery(id+"F0.wireOp",EDGE,"E2.5.6.0"),sQuery(id+"F0.wireOp",EDGE,"E2.5.7.0"),sQuery(id+"F0.wireOp",EDGE,"E2.5.8.0"),sQuery(id+"F0.wireOp",EDGE,"E2.5.9.0"),sQuery(id+"F0.wireOp",EDGE,"E2.6.0.0"),sQuery(id+"F0.wireOp",EDGE,"E2.6.1.0"),sQuery(id+"F0.wireOp",EDGE,"E2.6.2.0"),sQuery(id+"F0.wireOp",EDGE,"E2.6.3.0"),sQuery(id+"F0.wireOp",EDGE,"E2.6.4.0"),sQuery(id+"F0.wireOp",EDGE,"E2.6.5.0"),sQuery(id+"F0.wireOp",EDGE,"E2.6.6.0"),sQuery(id+"F0.wireOp",EDGE,"E2.6.7.0"),sQuery(id+"F0.wireOp",EDGE,"E2.6.8.0"),sQuery(id+"F0.wireOp",EDGE,"E2.6.9.0"),sQuery(id+"F0.wireOp",EDGE,"E2.7.0.0"),sQuery(id+"F0.wireOp",EDGE,"E2.7.1.0"),sQuery(id+"F0.wireOp",EDGE,"E2.7.2.0"),sQuery(id+"F0.wireOp",EDGE,"E2.7.3.0"),sQuery(id+"F0.wireOp",EDGE,"E2.7.4.0"),sQuery(id+"F0.wireOp",EDGE,"E2.7.5.0"),sQuery(id+"F0.wireOp",EDGE,"E2.7.6.0"),sQuery(id+"F0.wireOp",EDGE,"E2.7.7.0"),sQuery(id+"F0.wireOp",EDGE,"E2.7.8.0"),sQuery(id+"F0.wireOp",EDGE,"E2.7.9.0"),sQuery(id+"F0.wireOp",EDGE,"E2.8.0.0"),sQuery(id+"F0.wireOp",EDGE,"E2.8.1.0"),sQuery(id+"F0.wireOp",EDGE,"E2.8.2.0"),sQuery(id+"F0.wireOp",EDGE,"E2.8.3.0"),sQuery(id+"F0.wireOp",EDGE,"E2.8.4.0"),sQuery(id+"F0.wireOp",EDGE,"E2.8.5.0"),sQuery(id+"F0.wireOp",EDGE,"E2.8.6.0"),sQuery(id+"F0.wireOp",EDGE,"E2.8.7.0"),sQuery(id+"F0.wireOp",EDGE,"E2.8.8.0"),sQuery(id+"F0.wireOp",EDGE,"E2.8.9.0"),sQuery(id+"F0.wireOp",EDGE,"E2.9.0.0"),sQuery(id+"F0.wireOp",EDGE,"E2.9.1.0"),sQuery(id+"F0.wireOp",EDGE,"E2.9.2.0"),sQuery(id+"F0.wireOp",EDGE,"E2.9.3.0"),sQuery(id+"F0.wireOp",EDGE,"E2.9.4.0"),sQuery(id+"F0.wireOp",EDGE,"E2.9.5.0"),sQuery(id+"F0.wireOp",EDGE,"E2.9.6.0"),sQuery(id+"F0.wireOp",EDGE,"E2.9.7.0"),sQuery(id+"F0.wireOp",EDGE,"E2.9.8.0"),sQuery(id+"F0.wireOp",EDGE,"E2.9.9.0"),sQuery(id+"F0.wireOp",EDGE,"E2.10.0.0"),sQuery(id+"F0.wireOp",EDGE,"E2.10.1.0"),sQuery(id+"F0.wireOp",EDGE,"E2.10.2.0"),sQuery(id+"F0.wireOp",EDGE,"E2.10.3.0"),sQuery(id+"F0.wireOp",EDGE,"E2.10.4.0"),sQuery(id+"F0.wireOp",EDGE,"E2.10.5.0"),sQuery(id+"F0.wireOp",EDGE,"E2.10.6.0"),sQuery(id+"F0.wireOp",EDGE,"E2.10.7.0"),sQuery(id+"F0.wireOp",EDGE,"E2.10.8.0"),sQuery(id+"F0.wireOp",EDGE,"E2.10.9.0"),sQuery(id+"F0.wireOp",EDGE,"E2.11.0.0"),sQuery(id+"F0.wireOp",EDGE,"E2.11.1.0"),sQuery(id+"F0.wireOp",EDGE,"E2.11.2.0"),sQuery(id+"F0.wireOp",EDGE,"E2.11.3.0"),sQuery(id+"F0.wireOp",EDGE,"E2.11.4.0"),sQuery(id+"F0.wireOp",EDGE,"E2.11.5.0"),sQuery(id+"F0.wireOp",EDGE,"E2.11.6.0"),sQuery(id+"F0.wireOp",EDGE,"E2.11.7.0"),sQuery(id+"F0.wireOp",EDGE,"E2.11.8.0"),sQuery(id+"F0.wireOp",EDGE,"E2.11.9.0"),sQuery(id+"F0.wireOp",EDGE,"E2.12.0.0"),sQuery(id+"F0.wireOp",EDGE,"E2.12.1.0"),sQuery(id+"F0.wireOp",EDGE,"E2.12.2.0"),sQuery(id+"F0.wireOp",EDGE,"E2.12.3.0"),sQuery(id+"F0.wireOp",EDGE,"E2.12.4.0"),sQuery(id+"F0.wireOp",EDGE,"E2.12.5.0"),sQuery(id+"F0.wireOp",EDGE,"E2.12.6.0"),sQuery(id+"F0.wireOp",EDGE,"E2.12.7.0"),sQuery(id+"F0.wireOp",EDGE,"E2.12.8.0"),sQuery(id+"F0.wireOp",EDGE,"E2.12.9.0"),sQuery(id+"F0.wireOp",EDGE,"E2.13.0.0"),sQuery(id+"F0.wireOp",EDGE,"E2.13.1.0"),sQuery(id+"F0.wireOp",EDGE,"E2.13.2.0"),sQuery(id+"F0.wireOp",EDGE,"E2.13.3.0"),sQuery(id+"F0.wireOp",EDGE,"E2.13.4.0"),sQuery(id+"F0.wireOp",EDGE,"E2.13.5.0"),sQuery(id+"F0.wireOp",EDGE,"E2.13.6.0"),sQuery(id+"F0.wireOp",EDGE,"E2.13.7.0"),sQuery(id+"F0.wireOp",EDGE,"E2.13.8.0"),sQuery(id+"F0.wireOp",EDGE,"E2.13.9.0"),sQuery(id+"F0.wireOp",EDGE,"E2.14.0.0"),sQuery(id+"F0.wireOp",EDGE,"E2.14.1.0"),sQuery(id+"F0.wireOp",EDGE,"E2.14.2.0"),sQuery(id+"F0.wireOp",EDGE,"E2.14.3.0"),sQuery(id+"F0.wireOp",EDGE,"E2.14.4.0"),sQuery(id+"F0.wireOp",EDGE,"E2.14.5.0"),sQuery(id+"F0.wireOp",EDGE,"E2.14.6.0"),sQuery(id+"F0.wireOp",EDGE,"E2.14.7.0"),sQuery(id+"F0.wireOp",EDGE,"E2.14.8.0"),sQuery(id+"F0.wireOp",EDGE,"E2.14.9.0"),sQuery(id+"F0.wireOp",EDGE,"E2.15.0.0"),sQuery(id+"F0.wireOp",EDGE,"E2.15.1.0"),sQuery(id+"F0.wireOp",EDGE,"E2.15.2.0"),sQuery(id+"F0.wireOp",EDGE,"E2.15.3.0"),sQuery(id+"F0.wireOp",EDGE,"E2.15.4.0"),sQuery(id+"F0.wireOp",EDGE,"E2.15.5.0"),sQuery(id+"F0.wireOp",EDGE,"E2.15.6.0"),sQuery(id+"F0.wireOp",EDGE,"E2.15.7.0"),sQuery(id+"F0.wireOp",EDGE,"E2.15.8.0"),sQuery(id+"F0.wireOp",EDGE,"E2.15.9.0"),sQuery(id+"F0.wireOp",EDGE,"E2.16.0.0"),sQuery(id+"F0.wireOp",EDGE,"E2.16.1.0"),sQuery(id+"F0.wireOp",EDGE,"E2.16.2.0"),sQuery(id+"F0.wireOp",EDGE,"E2.16.3.0"),sQuery(id+"F0.wireOp",EDGE,"E2.16.4.0"),sQuery(id+"F0.wireOp",EDGE,"E2.16.5.0"),sQuery(id+"F0.wireOp",EDGE,"E2.16.6.0"),sQuery(id+"F0.wireOp",EDGE,"E2.16.7.0"),sQuery(id+"F0.wireOp",EDGE,"E2.16.8.0"),sQuery(id+"F0.wireOp",EDGE,"E2.16.9.0"),sQuery(id+"F0.wireOp",EDGE,"E2.17.0.0"),sQuery(id+"F0.wireOp",EDGE,"E2.17.1.0"),sQuery(id+"F0.wireOp",EDGE,"E2.17.2.0"),sQuery(id+"F0.wireOp",EDGE,"E2.17.3.0"),sQuery(id+"F0.wireOp",EDGE,"E2.17.4.0"),sQuery(id+"F0.wireOp",EDGE,"E2.17.5.0"),sQuery(id+"F0.wireOp",EDGE,"E2.17.6.0"),sQuery(id+"F0.wireOp",EDGE,"E2.17.7.0"),sQuery(id+"F0.wireOp",EDGE,"E2.17.8.0"),sQuery(id+"F0.wireOp",EDGE,"E2.17.9.0"),sQuery(id+"F0.wireOp",EDGE,"E2.18.0.0"),sQuery(id+"F0.wireOp",EDGE,"E2.18.1.0"),sQuery(id+"F0.wireOp",EDGE,"E2.18.2.0"),sQuery(id+"F0.wireOp",EDGE,"E2.18.3.0"),sQuery(id+"F0.wireOp",EDGE,"E2.18.4.0"),sQuery(id+"F0.wireOp",EDGE,"E2.18.5.0"),sQuery(id+"F0.wireOp",EDGE,"E2.18.6.0"),sQuery(id+"F0.wireOp",EDGE,"E2.18.7.0"),sQuery(id+"F0.wireOp",EDGE,"E2.18.8.0"),sQuery(id+"F0.wireOp",EDGE,"E2.18.9.0"),sQuery(id+"F0.wireOp",EDGE,"E2.19.0.0"),sQuery(id+"F0.wireOp",EDGE,"E2.19.1.0"),sQuery(id+"F0.wireOp",EDGE,"E2.19.2.0"),sQuery(id+"F0.wireOp",EDGE,"E2.19.3.0"),sQuery(id+"F0.wireOp",EDGE,"E2.19.4.0"),sQuery(id+"F0.wireOp",EDGE,"E2.19.5.0"),sQuery(id+"F0.wireOp",EDGE,"E2.19.6.0"),sQuery(id+"F0.wireOp",EDGE,"E2.19.7.0"),sQuery(id+"F0.wireOp",EDGE,"E2.19.8.0"),sQuery(id+"F0.wireOp",EDGE,"E2.19.9.0")])]});
            hole(context, id + "F5", {"style" : HoleStyle.SIMPLE, "endStyle" : HoleEndStyle.THROUGH, "holeDiameter" : 5 * mm, "isTappedThrough" : true, "tappedDepth" : 12 * mm, "tapClearance" : 3, "locations" : qUnion([Q0]), "scope" : qUnion([Q1])});
        }
    });
